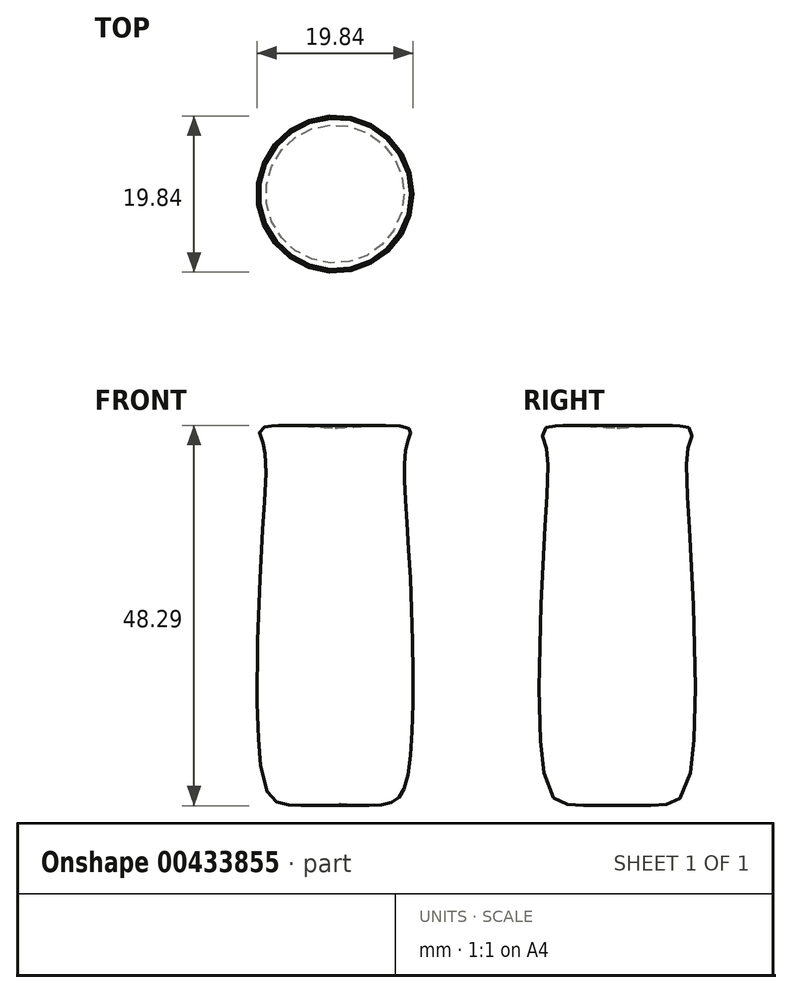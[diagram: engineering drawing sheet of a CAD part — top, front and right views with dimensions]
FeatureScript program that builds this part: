
annotation { "Feature Type Name" : "Feature", "Feature Type Description" : "" }
export const myFeature = defineFeature(function(context is Context, id is Id, definition is map)
    precondition{}
    {
        {
            var Q0;
            Q0=qCreatedBy(makeId("Front.planeOp"),FACE);
            var sketch = newSketch(context, id + "F0", { "sketchPlane" : qUnion([Q0])});
            skFitSpline(sketch, "E0", {"points": [v(0, 47.7) * mm, v(9.52, 47.5) * mm, v(9.13, 45.77) * mm, v(9.33, 32.7) * mm, v(9.13, 3.08) * mm, v(6.83, 0) * mm, v(0, 0) * mm], "startDerivative": vector(77.7, 5.34) * mm, "endDerivative": vector(-54, 4.99) * mm});
            skLineSegment(sketch, "E1", {"start": v(0, 47.7) * mm, "end": v(0, 0) * mm});
            skSolve(sketch);
        }
        {
            var Q0;
            Q0 = qSketchRegion(id + "F0", true);
            var Q1;
            Q1=sQuery(id+"F0.wireOp",EDGE,"E1");
            revolve(context, id + "F1", {"entities" : qUnion([Q0]), "axis" : qUnion([Q1]), "revolveType" : RevolveType.FULL});
        }
    });
